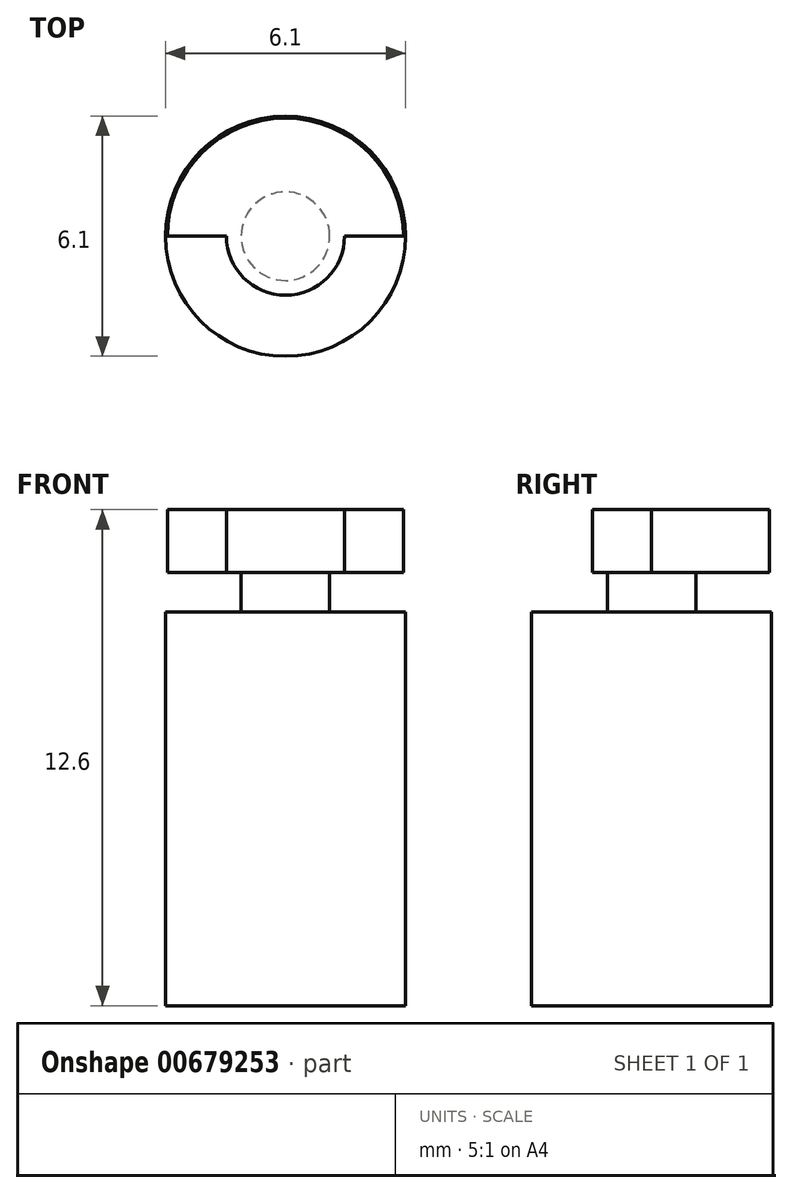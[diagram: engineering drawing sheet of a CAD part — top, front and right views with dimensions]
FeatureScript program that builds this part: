
annotation { "Feature Type Name" : "Feature", "Feature Type Description" : "" }
export const myFeature = defineFeature(function(context is Context, id is Id, definition is map)
    precondition{}
    {
        {
            assignVariable(context, id + "F0", {"name" : "motorlength", "anyValue" : 10});
        }
        {
            assignVariable(context, id + "F1", {"name" : "axlelength", "anyValue" : 1});
        }
        {
            assignVariable(context, id + "F2", {"name" : "offsetweightthick", "anyValue" : 1.6});
        }
        {
            var Q0;
            Q0=qCreatedBy(makeId("Top.planeOp"),FACE);
            var sketch = newSketch(context, id + "F3", { "sketchPlane" : qUnion([Q0])});
            skCircle(sketch, "E0", {"center": v(0, 0) * mm, "radius": 3.05 * mm});
            skSolve(sketch);
        }
        {
            var Q0;
            Q0 = qSketchRegion(id + "F3", true);
            extrude(context, id + "F4", {"entities" : qUnion([Q0]), "depth" : (getVariable(context, 'motorlength')) * mm, "offsetDistance" : 25 * mm});
        }
        {
            var Q0;
            Q0=makeQuery(id+"F4.opExtrude","CAP_FACE",FACE,{"disambiguationData":[OSD([sQuery(id+"F3.wireOp",EDGE,"E0")])],"isStart":false});
            var sketch = newSketch(context, id + "F5", { "sketchPlane" : qUnion([Q0])});
            skCircle(sketch, "E1", {"center": v(0, 0) * mm, "radius": 1.13 * mm});
            skSolve(sketch);
        }
        {
            var Q0;
            Q0 = qSketchRegion(id + "F5", true);
            extrude(context, id + "F6", {"entities" : qUnion([Q0]), "operationType" : NewBodyOperationType.ADD, "depth" : (getVariable(context, 'axlelength')) * mm, "offsetDistance" : 25 * mm});
        }
        {
            var Q0;
            Q0=makeQuery(id+"F6.opExtrude","CAP_FACE",FACE,{"disambiguationData":[OSD([sQuery(id+"F5.wireOp",EDGE,"E1")])],"isStart":false});
            var sketch = newSketch(context, id + "F7", { "sketchPlane" : qUnion([Q0])});
            skLineSegment(sketch, "E2", {"start": v(-3, 0) * mm, "end": v(3, 0) * mm});
            skArc(sketch, "E3", {"start": v(3, 0) * mm, "mid": v(0, 3) * mm, "end": v(-3, 0) * mm});
            skArc(sketch, "E4", {"start": v(-1.5, 0) * mm, "mid": v(0, -1.5) * mm, "end": v(1.5, 0) * mm});
            skSolve(sketch);
        }
        {
            var Q0;
            Q0 = qSketchRegion(id + "F7", true);
            extrude(context, id + "F8", {"entities" : qUnion([Q0]), "operationType" : NewBodyOperationType.ADD, "depth" : (getVariable(context, 'offsetweightthick')) * mm, "offsetDistance" : 25 * mm});
        }
    });
